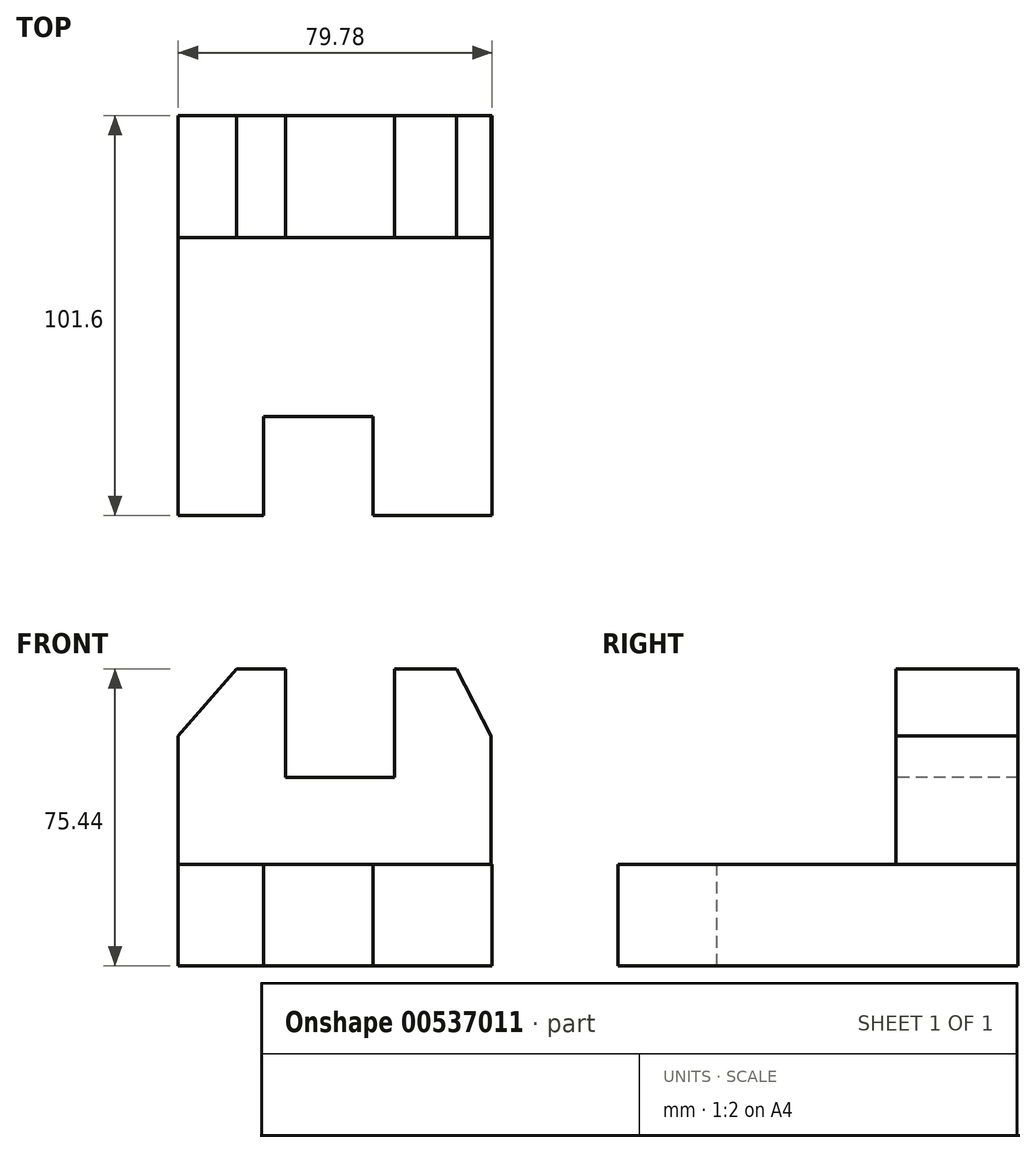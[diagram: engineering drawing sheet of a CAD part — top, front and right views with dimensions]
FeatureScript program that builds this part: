
annotation { "Feature Type Name" : "Feature", "Feature Type Description" : "" }
export const myFeature = defineFeature(function(context is Context, id is Id, definition is map)
    precondition{}
    {
        {
            var Q0;
            Q0=qCreatedBy(makeId("Top.planeOp"),FACE);
            var sketch = newSketch(context, id + "F0", { "sketchPlane" : qUnion([Q0])});
            skLineSegment(sketch, "E0.bottom", {"start": v(0, 0) * mm, "end": v(-101.6, 0) * mm});
            skLineSegment(sketch, "E0.top", {"start": v(0, -101.6) * mm, "end": v(-101.6, -101.6) * mm});
            skLineSegment(sketch, "E0.left", {"start": v(0, 0) * mm, "end": v(0, -101.6) * mm});
            skLineSegment(sketch, "E0.right", {"start": v(-101.6, 0) * mm, "end": v(-101.6, -101.6) * mm});
            skSolve(sketch);
        }
        {
            var Q0;
            Q0 = qSketchRegion(id + "F0", true);
            extrude(context, id + "F1", {"entities" : qUnion([Q0]), "depth" : 75.44 * mm, "offsetDistance" : 25.4 * mm});
        }
        {
            var Q0;
            Q0=makeQuery(id+"F1.opExtrude","SWEPT_FACE",FACE,{"disambiguationData":[OSD([sQuery(id+"F0.wireOp",EDGE,"E0.top")])]});
            var sketch = newSketch(context, id + "F2", { "sketchPlane" : qUnion([Q0])});
            skLineSegment(sketch, "E1.bottom", {"start": v(-71.6, 0) * mm, "end": v(-43.56, 0) * mm});
            skLineSegment(sketch, "E1.top", {"start": v(-71.6, -9.15) * mm, "end": v(-43.56, -9.15) * mm});
            skLineSegment(sketch, "E1.left", {"start": v(-71.6, -9.15) * mm, "end": v(-71.6, 0) * mm});
            skLineSegment(sketch, "E1.right", {"start": v(-43.56, -9.15) * mm, "end": v(-43.56, 0) * mm});
            skSolve(sketch);
        }
        {
            var Q0;
            Q0 = qSketchRegion(id + "F2", true);
            extrude(context, id + "F3", {"entities" : qUnion([Q0]), "operationType" : NewBodyOperationType.REMOVE, "oppositeDirection" : true, "depth" : 25.4 * mm, "offsetDistance" : 25.4 * mm});
        }
        {
            var Q0;
            Q0=makeQuery(id+"F1.opExtrude","SWEPT_FACE",FACE,{"disambiguationData":[OSD([sQuery(id+"F0.wireOp",EDGE,"E0.top")])]});
            var sketch = newSketch(context, id + "F4", { "sketchPlane" : qUnion([Q0])});
            skLineSegment(sketch, "E2.bottom", {"start": v(-101.6, 25.78) * mm, "end": v(0, 25.78) * mm});
            skLineSegment(sketch, "E2.top", {"start": v(-101.6, 75.44) * mm, "end": v(0, 75.44) * mm});
            skLineSegment(sketch, "E2.left", {"start": v(-101.6, 25.78) * mm, "end": v(-101.6, 75.44) * mm});
            skLineSegment(sketch, "E2.right", {"start": v(0, 25.78) * mm, "end": v(0, 75.44) * mm});
            skSolve(sketch);
        }
        {
            var Q0;
            Q0 = qSketchRegion(id + "F4", true);
            extrude(context, id + "F5", {"entities" : qUnion([Q0]), "operationType" : NewBodyOperationType.REMOVE, "oppositeDirection" : true, "depth" : 70.61 * mm, "offsetDistance" : 25.4 * mm});
        }
        {
            var Q0;
            Q0=makeQuery(id+"F1.opExtrude","SWEPT_FACE",FACE,{"disambiguationData":[OSD([sQuery(id+"F0.wireOp",EDGE,"E0.top")])]});
            var sketch = newSketch(context, id + "F6", { "sketchPlane" : qUnion([Q0])});
            skLineSegment(sketch, "E3.bottom", {"start": v(-71.6, 0.25) * mm, "end": v(-43.72, 0.25) * mm});
            skLineSegment(sketch, "E3.top", {"start": v(-71.6, 25.78) * mm, "end": v(-43.72, 25.78) * mm});
            skLineSegment(sketch, "E3.left", {"start": v(-71.6, 0.25) * mm, "end": v(-71.6, 25.78) * mm});
            skLineSegment(sketch, "E3.right", {"start": v(-43.72, 0.25) * mm, "end": v(-43.72, 25.78) * mm});
            skSolve(sketch);
        }
        {
            var Q0;
            Q0 = qSketchRegion(id + "F6", true);
            extrude(context, id + "F7", {"entities" : qUnion([Q0]), "operationType" : NewBodyOperationType.REMOVE, "oppositeDirection" : true, "depth" : 25.15 * mm, "offsetDistance" : 25.4 * mm});
        }
        {
            var Q0;
            Q0=makeQuery(id+"F5.boolean.opBoolean","COPY",FACE,{"derivedFrom":makeQuery(id+"F5.opExtrude","CAP_FACE",FACE,{"disambiguationData":[OSD([sQuery(id+"F4.wireOp",EDGE,"E2.bottom"),sQuery(id+"F4.wireOp",EDGE,"E2.top"),sQuery(id+"F4.wireOp",EDGE,"E2.left"),sQuery(id+"F4.wireOp",EDGE,"E2.right")])],"isStart":false})});
            var sketch = newSketch(context, id + "F8", { "sketchPlane" : qUnion([Q0])});
            skLineSegment(sketch, "E4", {"start": v(-78.4, 75.44) * mm, "end": v(-93.24, 58.49) * mm});
            skLineSegment(sketch, "E5", {"start": v(-93.24, 58.49) * mm, "end": v(-93.24, 25.78) * mm});
            skLineSegment(sketch, "E6", {"start": v(-22.34, 75.44) * mm, "end": v(-14.42, 58.49) * mm});
            skLineSegment(sketch, "E7", {"start": v(-14.42, 58.49) * mm, "end": v(-14.42, 25.78) * mm});
            skSolve(sketch);
        }
        {
            var Q0;
            Q0 = qSketchRegion(id + "F8", true);
            var Q1;
            {var subQ3=sQuery(id+"F8.wireOp",EDGE,"E4");Q1=makeQuery(id+"F8.imprint","IMPRINT",FACE,{"disambiguationData":[TD([[makeQuery(id+"F8.imprint","IMPRINT",EDGE,{"derivedFrom":subQ3}),-1.0]])]});}
            extrude(context, id + "F9", {"entities" : qUnion([Q0, Q1]), "operationType" : NewBodyOperationType.REMOVE, "oppositeDirection" : true, "depth" : 68.07 * mm, "offsetDistance" : 25.4 * mm});
        }
        {
            var Q0;
            Q0=makeQuery(id+"F7.boolean.opBoolean","COPY",FACE,{"derivedFrom":makeQuery(id+"F7.opExtrude","SWEPT_FACE",FACE,{"disambiguationData":[OSD([sQuery(id+"F6.wireOp",EDGE,"E3.bottom")])]})});
            extrude(context, id + "F10", {"entities" : qUnion([Q0]), "operationType" : NewBodyOperationType.REMOVE, "oppositeDirection" : true, "depth" : 25.4 * mm, "offsetDistance" : 25.4 * mm});
        }
        {
            var Q0;
            Q0=makeQuery(id+"F5.boolean.opBoolean","COPY",FACE,{"derivedFrom":makeQuery(id+"F5.opExtrude","CAP_FACE",FACE,{"disambiguationData":[OSD([sQuery(id+"F4.wireOp",EDGE,"E2.bottom"),sQuery(id+"F4.wireOp",EDGE,"E2.top"),sQuery(id+"F4.wireOp",EDGE,"E2.left"),sQuery(id+"F4.wireOp",EDGE,"E2.right")])],"isStart":false})});
            var sketch = newSketch(context, id + "F11", { "sketchPlane" : qUnion([Q0])});
            skLineSegment(sketch, "E8", {"start": v(-22.55, 75.44) * mm, "end": v(-13.78, 58.49) * mm});
            skLineSegment(sketch, "E9", {"start": v(-13.78, 58.49) * mm, "end": v(-13.78, 25.78) * mm});
            skSolve(sketch);
        }
        {
            var Q0;
            Q0 = qSketchRegion(id + "F11", true);
            var Q1;
            {var subQ3=sQuery(id+"F11.wireOp",EDGE,"E8");Q1=makeQuery(id+"F11.imprint","IMPRINT",FACE,{"disambiguationData":[TD([[makeQuery(id+"F11.imprint","IMPRINT",EDGE,{"derivedFrom":subQ3}),1.0]])]});}
            extrude(context, id + "F12", {"entities" : qUnion([Q0, Q1]), "operationType" : NewBodyOperationType.REMOVE, "oppositeDirection" : true, "depth" : 60.96 * mm, "offsetDistance" : 25.4 * mm});
        }
        {
            var Q0;
            Q0=makeQuery(id+"F5.boolean.opBoolean","COPY",FACE,{"derivedFrom":makeQuery(id+"F5.opExtrude","CAP_FACE",FACE,{"disambiguationData":[OSD([sQuery(id+"F4.wireOp",EDGE,"E2.bottom"),sQuery(id+"F4.wireOp",EDGE,"E2.top"),sQuery(id+"F4.wireOp",EDGE,"E2.left"),sQuery(id+"F4.wireOp",EDGE,"E2.right")])],"isStart":false})});
            var sketch = newSketch(context, id + "F13", { "sketchPlane" : qUnion([Q0])});
            skLineSegment(sketch, "E10.bottom", {"start": v(-65.9, 75.44) * mm, "end": v(-38.23, 75.44) * mm});
            skLineSegment(sketch, "E10.top", {"start": v(-65.9, 47.9) * mm, "end": v(-38.23, 47.9) * mm});
            skLineSegment(sketch, "E10.left", {"start": v(-65.9, 75.44) * mm, "end": v(-65.9, 47.9) * mm});
            skLineSegment(sketch, "E10.right", {"start": v(-38.23, 75.44) * mm, "end": v(-38.23, 47.9) * mm});
            skSolve(sketch);
        }
        {
            var Q0;
            Q0 = qSketchRegion(id + "F13", true);
            extrude(context, id + "F14", {"entities" : qUnion([Q0]), "operationType" : NewBodyOperationType.REMOVE, "oppositeDirection" : true, "depth" : 72.14 * mm, "offsetDistance" : 25.4 * mm});
        }
        {
            var Q0;
            Q0=makeQuery(id+"F1.opExtrude","SWEPT_FACE",FACE,{"disambiguationData":[OSD([sQuery(id+"F0.wireOp",EDGE,"E0.left")])]});
            extrude(context, id + "F15", {"entities" : qUnion([Q0]), "operationType" : NewBodyOperationType.ADD, "oppositeDirection" : true, "depth" : 13.72 * mm, "offsetDistance" : 25.4 * mm});
        }
        {
            var Q0;
            Q0=makeQuery(id+"F1.opExtrude","SWEPT_FACE",FACE,{"disambiguationData":[OSD([sQuery(id+"F0.wireOp",EDGE,"E0.left")])]});
            extrude(context, id + "F16", {"entities" : qUnion([Q0]), "operationType" : NewBodyOperationType.REMOVE, "oppositeDirection" : true, "depth" : 13.46 * mm, "offsetDistance" : 25.4 * mm});
        }
        {
            var Q0;
            {var subQ0=sQuery(id+"F4.wireOp",EDGE,"E2.bottom");Q0=makeQuery(id+"F12.boolean.opBoolean","MERGE",FACE,{"derivedFrom":[makeQuery(id+"F9.boolean.opBoolean","MERGE",FACE,{"derivedFrom":[makeQuery(id+"F5.boolean.opBoolean","COPY",FACE,{"derivedFrom":makeQuery(id+"F5.opExtrude","SWEPT_FACE",FACE,{"disambiguationData":[OSD([subQ0])]})}),makeQuery(id+"F9.opExtrude","SWEPT_FACE",FACE,{"disambiguationData":[OSD([subQ0])]})]}),makeQuery(id+"F12.opExtrude","SWEPT_FACE",FACE,{"disambiguationData":[OSD([subQ0])]})]});}
            var sketch = newSketch(context, id + "F17", { "sketchPlane" : qUnion([Q0])});
            skLineSegment(sketch, "E11", {"start": v(-93.24, -30.99) * mm, "end": v(-93.24, -101.6) * mm});
            skLineSegment(sketch, "E12", {"start": v(-93.24, -101.6) * mm, "end": v(-68.08, -128.43) * mm});
            skSolve(sketch);
        }
        {
            var Q0;
            {var subQ5=sQuery(id+"F17.wireOp",EDGE,"E11");Q0=makeQuery(id+"F17.imprint","IMPRINT",FACE,{"disambiguationData":[TD([[makeQuery(id+"F17.imprint","IMPRINT",EDGE,{"derivedFrom":subQ5}),-1.0]])]});}
            extrude(context, id + "F18", {"entities" : qUnion([Q0]), "operationType" : NewBodyOperationType.REMOVE, "oppositeDirection" : true, "depth" : 43.43 * mm, "offsetDistance" : 25.4 * mm});
        }
    });
